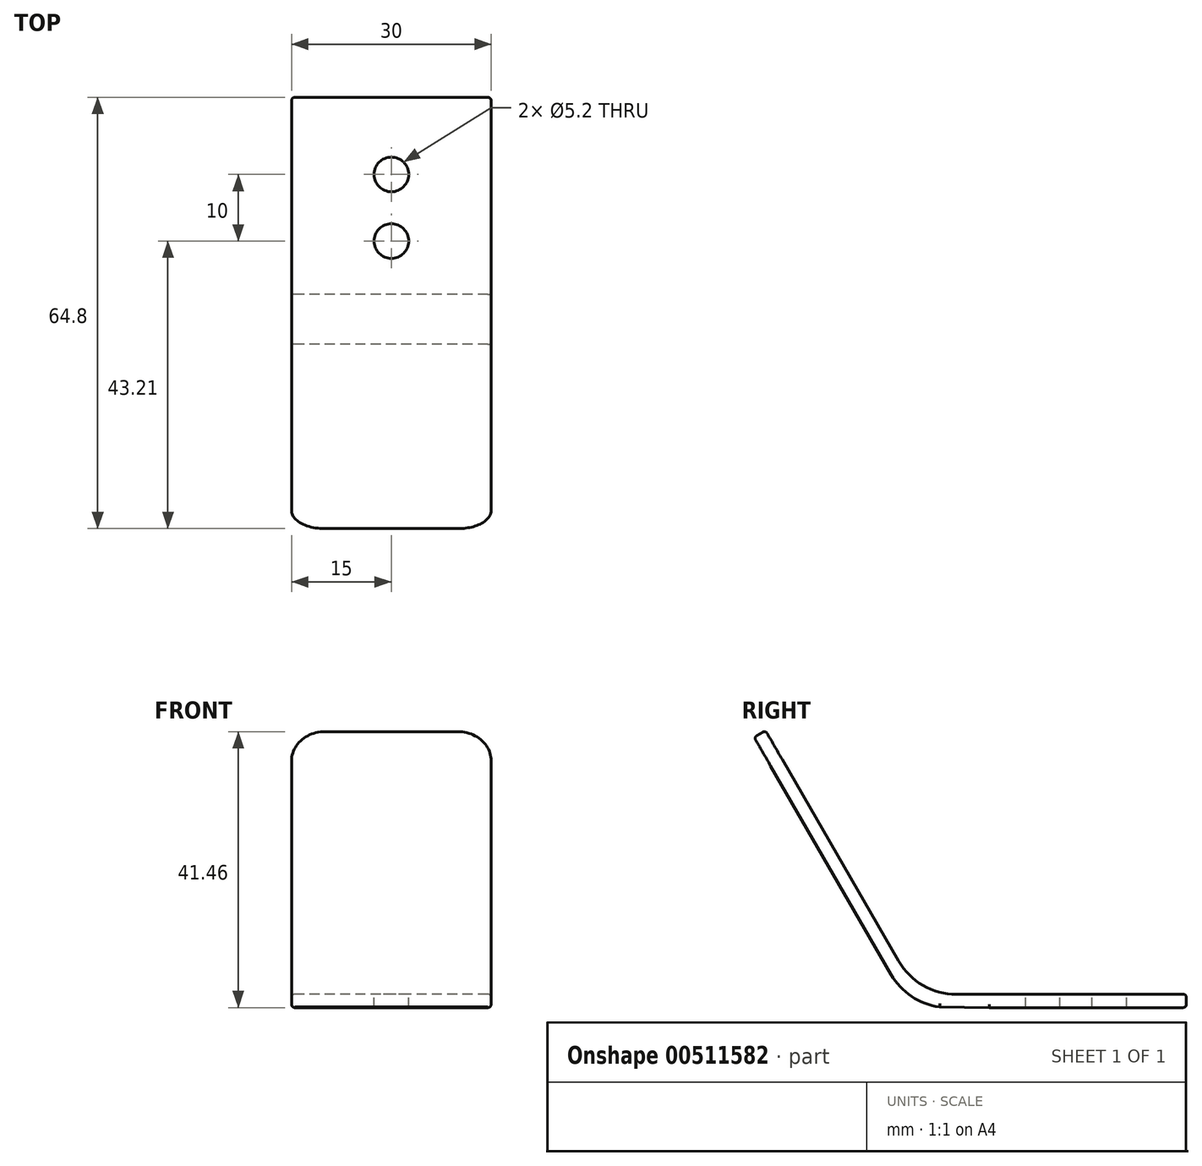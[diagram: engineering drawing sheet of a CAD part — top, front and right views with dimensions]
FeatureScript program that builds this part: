
annotation { "Feature Type Name" : "Feature", "Feature Type Description" : "" }
export const myFeature = defineFeature(function(context is Context, id is Id, definition is map)
    precondition{}
    {
        {
            var Q0;
            Q0=qCreatedBy(makeId("Right.planeOp"),FACE);
            var sketch = newSketch(context, id + "F0", { "sketchPlane" : qUnion([Q0])});
            skLineSegment(sketch, "E0", {"start": v(0, 0) * mm, "end": v(-5, 0) * mm});
            skArc(sketch, "E1", {"start": v(-13.66, 5) * mm, "mid": v(-10, 1.34) * mm, "end": v(-5, 0) * mm});
            skLineSegment(sketch, "E2", {"start": v(-13.66, 5) * mm, "end": v(-33.66, 39.64) * mm});
            skLineSegment(sketch, "E3", {"start": v(-33.66, 39.64) * mm, "end": v(-35.4, 38.64) * mm});
            skLineSegment(sketch, "E4", {"start": v(-35.4, 38.64) * mm, "end": v(-14.81, 3) * mm});
            skPoint(sketch, "E5.start.orphan", {"position": v(-13.66, 3) * mm});
            skPoint(sketch, "E6.end.orphan", {"position": v(-5, -2) * mm});
            skPoint(sketch, "E6.start.orphan", {"position": v(0, -2) * mm});
            skArc(sketch, "E7", {"start": v(-14.81, 3) * mm, "mid": v(-11.73, -0.3) * mm, "end": v(-7.5, -1.9) * mm});
            skLineSegment(sketch, "E8", {"start": v(-7.5, -1.9) * mm, "end": v(0, -2) * mm});
            skLineSegment(sketch, "E9", {"start": v(0, 0) * mm, "end": v(29.59, 0) * mm});
            skLineSegment(sketch, "E10", {"start": v(29.59, 0) * mm, "end": v(29.59, -2) * mm});
            skLineSegment(sketch, "E11", {"start": v(29.59, -2) * mm, "end": v(0, -2) * mm});
            skSolve(sketch);
        }
        {
            var Q0;
            Q0 = qSketchRegion(id + "F0", true);
            extrude(context, id + "F1", {"entities" : qUnion([Q0]), "depth" : 30 * mm});
        }
        {
            var Q0;
            Q0=makeQuery(id+"F1.opExtrude","SWEPT_FACE",FACE,{"disambiguationData":[OSD([sQuery(id+"F0.wireOp",EDGE,"E0"),sQuery(id+"F0.wireOp",EDGE,"E9")])]});
            var sketch = newSketch(context, id + "F2", { "sketchPlane" : qUnion([Q0])});
            skCircle(sketch, "E12", {"center": v(15, 18) * mm, "radius": 2.6 * mm});
            skPoint(sketch, "E12.centerSnap0", {"position": v(15, 29.59) * mm});
            skCircle(sketch, "E13", {"center": v(15, 8) * mm, "radius": 2.6 * mm});
            skSolve(sketch);
        }
        {
            var Q0;
            Q0 = qSketchRegion(id + "F2", true);
            extrude(context, id + "F3", {"entities" : qUnion([Q0]), "operationType" : NewBodyOperationType.REMOVE, "oppositeDirection" : true, "depth" : 25 * mm});
        }
        {
            var Q0;
            Q0=makeQuery(id+"F1.opExtrude","CAP_EDGE",EDGE,{"disambiguationData":[OSD([sQuery(id+"F0.wireOp",EDGE,"E3")])],"isStart":false});
            var Q1;
            Q1=makeQuery(id+"F1.opExtrude","CAP_EDGE",EDGE,{"disambiguationData":[OSD([sQuery(id+"F0.wireOp",EDGE,"E3")])],"isStart":true});
            fillet(context, id + "F4", {"entities" : qUnion([Q0, Q1]), "radius" : 5 * mm, "tangentPropagation" : true, "allowEdgeOverflow" : false});
        }
        {
            var Q0;
            Q0=makeQuery(id+"F1.opExtrude","CAP_EDGE",EDGE,{"disambiguationData":[OSD([sQuery(id+"F0.wireOp",EDGE,"E2")])],"isStart":false});
            var Q1;
            Q1=makeQuery(id+"F1.opExtrude","CAP_EDGE",EDGE,{"disambiguationData":[OSD([sQuery(id+"F0.wireOp",EDGE,"E4")])],"isStart":false});
            var Q2;
            Q2=makeQuery(id+"F4.opFillet","BLEND_EDGE",EDGE,{"blendedFrom":[makeQuery(id+"F1.opExtrude","CAP_EDGE",EDGE,{"disambiguationData":[OSD([sQuery(id+"F0.wireOp",EDGE,"E3")])],"isStart":true}),makeQuery(id+"F1.opExtrude","SWEPT_FACE",FACE,{"disambiguationData":[OSD([sQuery(id+"F0.wireOp",EDGE,"E2")])]})],"blendedInto":[makeQuery(id+"F1.opExtrude","SWEPT_FACE",FACE,{"disambiguationData":[OSD([sQuery(id+"F0.wireOp",EDGE,"E2")])]})]});
            var Q3;
            Q3=makeQuery(id+"F4.opFillet","BLEND_EDGE",EDGE,{"blendedFrom":[makeQuery(id+"F1.opExtrude","CAP_EDGE",EDGE,{"disambiguationData":[OSD([sQuery(id+"F0.wireOp",EDGE,"E3")])],"isStart":false}),makeQuery(id+"F1.opExtrude","SWEPT_FACE",FACE,{"disambiguationData":[OSD([sQuery(id+"F0.wireOp",EDGE,"E2")])]})],"blendedInto":[makeQuery(id+"F1.opExtrude","SWEPT_FACE",FACE,{"disambiguationData":[OSD([sQuery(id+"F0.wireOp",EDGE,"E2")])]})]});
            var Q4;
            Q4=makeQuery(id+"F4.opFillet","BLEND_EDGE",EDGE,{"blendedFrom":[makeQuery(id+"F1.opExtrude","CAP_EDGE",EDGE,{"disambiguationData":[OSD([sQuery(id+"F0.wireOp",EDGE,"E3")])],"isStart":false}),makeQuery(id+"F1.opExtrude","SWEPT_FACE",FACE,{"disambiguationData":[OSD([sQuery(id+"F0.wireOp",EDGE,"E4")])]})],"blendedInto":[makeQuery(id+"F1.opExtrude","SWEPT_FACE",FACE,{"disambiguationData":[OSD([sQuery(id+"F0.wireOp",EDGE,"E4")])]})]});
            var Q5;
            Q5=makeQuery(id+"F4.opFillet","BLEND_EDGE",EDGE,{"blendedFrom":[makeQuery(id+"F1.opExtrude","CAP_EDGE",EDGE,{"disambiguationData":[OSD([sQuery(id+"F0.wireOp",EDGE,"E3")])],"isStart":true}),makeQuery(id+"F1.opExtrude","SWEPT_FACE",FACE,{"disambiguationData":[OSD([sQuery(id+"F0.wireOp",EDGE,"E4")])]})],"blendedInto":[makeQuery(id+"F1.opExtrude","SWEPT_FACE",FACE,{"disambiguationData":[OSD([sQuery(id+"F0.wireOp",EDGE,"E4")])]})]});
            var Q6;
            Q6=makeQuery(id+"F1.opExtrude","CAP_EDGE",EDGE,{"disambiguationData":[OSD([sQuery(id+"F0.wireOp",EDGE,"E2")])],"isStart":true});
            var Q7;
            Q7=makeQuery(id+"F1.opExtrude","CAP_EDGE",EDGE,{"disambiguationData":[OSD([sQuery(id+"F0.wireOp",EDGE,"E4")])],"isStart":true});
            var Q8;
            Q8=makeQuery(id+"F1.opExtrude","CAP_EDGE",EDGE,{"disambiguationData":[OSD([sQuery(id+"F0.wireOp",EDGE,"E7")])],"isStart":true});
            var Q9;
            Q9=makeQuery(id+"F1.opExtrude","CAP_EDGE",EDGE,{"disambiguationData":[OSD([sQuery(id+"F0.wireOp",EDGE,"E1")])],"isStart":true});
            var Q10;
            Q10=makeQuery(id+"F1.opExtrude","CAP_EDGE",EDGE,{"disambiguationData":[OSD([sQuery(id+"F0.wireOp",EDGE,"E8")])],"isStart":true});
            var Q11;
            Q11=makeQuery(id+"F1.opExtrude","CAP_EDGE",EDGE,{"disambiguationData":[OSD([sQuery(id+"F0.wireOp",EDGE,"E0"),sQuery(id+"F0.wireOp",EDGE,"E9")])],"isStart":true});
            var Q12;
            Q12=makeQuery(id+"F1.opExtrude","CAP_EDGE",EDGE,{"disambiguationData":[OSD([sQuery(id+"F0.wireOp",EDGE,"E11")])],"isStart":true});
            var Q13;
            Q13=makeQuery(id+"F1.opExtrude","SWEPT_EDGE",EDGE,{"disambiguationData":[OSD([sQuery(id+"F0.wireOp",EDGE,"E3"),sQuery(id+"F0.wireOp",EDGE,"E4")])]});
            var Q14;
            Q14=makeQuery(id+"F1.opExtrude","SWEPT_EDGE",EDGE,{"disambiguationData":[OSD([sQuery(id+"F0.wireOp",EDGE,"E2"),sQuery(id+"F0.wireOp",EDGE,"E3")])]});
            var Q15;
            Q15=makeQuery(id+"F1.opExtrude","CAP_EDGE",EDGE,{"disambiguationData":[OSD([sQuery(id+"F0.wireOp",EDGE,"E7")])],"isStart":false});
            var Q16;
            Q16=makeQuery(id+"F1.opExtrude","CAP_EDGE",EDGE,{"disambiguationData":[OSD([sQuery(id+"F0.wireOp",EDGE,"E1")])],"isStart":false});
            var Q17;
            Q17=makeQuery(id+"F1.opExtrude","CAP_EDGE",EDGE,{"disambiguationData":[OSD([sQuery(id+"F0.wireOp",EDGE,"E0"),sQuery(id+"F0.wireOp",EDGE,"E9")])],"isStart":false});
            var Q18;
            Q18=makeQuery(id+"F1.opExtrude","CAP_EDGE",EDGE,{"disambiguationData":[OSD([sQuery(id+"F0.wireOp",EDGE,"E8")])],"isStart":false});
            var Q19;
            Q19=makeQuery(id+"F1.opExtrude","CAP_EDGE",EDGE,{"disambiguationData":[OSD([sQuery(id+"F0.wireOp",EDGE,"E11")])],"isStart":false});
            var Q20;
            Q20=makeQuery(id+"F1.opExtrude","SWEPT_EDGE",EDGE,{"disambiguationData":[OSD([sQuery(id+"F0.wireOp",EDGE,"E9"),sQuery(id+"F0.wireOp",EDGE,"E10")])]});
            var Q21;
            Q21=makeQuery(id+"F1.opExtrude","SWEPT_EDGE",EDGE,{"disambiguationData":[OSD([sQuery(id+"F0.wireOp",EDGE,"E10"),sQuery(id+"F0.wireOp",EDGE,"E11")])]});
            var Q22;
            Q22=makeQuery(id+"F1.opExtrude","CAP_EDGE",EDGE,{"disambiguationData":[OSD([sQuery(id+"F0.wireOp",EDGE,"E10")])],"isStart":false});
            var Q23;
            Q23=makeQuery(id+"F1.opExtrude","CAP_EDGE",EDGE,{"disambiguationData":[OSD([sQuery(id+"F0.wireOp",EDGE,"E10")])],"isStart":true});
            fillet(context, id + "F5", {"entities" : qUnion([Q0, Q1, Q2, Q3, Q4, Q5, Q6, Q7, Q8, Q9, Q10, Q11, Q12, Q13, Q14, Q15, Q16, Q17, Q18, Q19, Q20, Q21, Q22, Q23]), "radius" : 0.5 * mm, "tangentPropagation" : true, "allowEdgeOverflow" : false});
        }
    });
